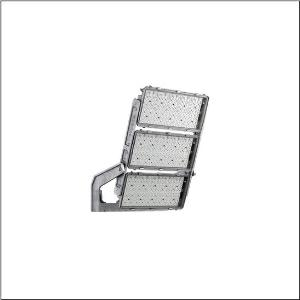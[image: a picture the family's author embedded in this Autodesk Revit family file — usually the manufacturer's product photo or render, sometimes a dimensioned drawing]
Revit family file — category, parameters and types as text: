
# Revit family: floodlight_fl_11_maxi_pro_remote___pl33t_5xa779425t01aa_7d4a
name_source: partatom
category: Lighting Fixtures
units: mm (PartAtom-declared; Revit-internal decimal feet)

## family parameters
Cut with Voids When Loaded = No
Host = Face
Light Source = No
Part Type = Normal
Room Calculation Point = No
Round Connector Dimension = Use Diameter
Shared = No

## types (1)
- --- (1 x LED, 201910 lm, 1539.3 W, 3000K)
    Apparent Load = 1539 VA
    CIE Flux Codes = 27 70 98 100 100
    Color Rendering = 70
    Color Temperature = 3000K
    Default Elevation = 1800 mm
    Description = Floodlight FL 11  maxi  pro Remote floodlight; light control with lens of PMMA; cover panel of toughened safety glass, transparent; light distribution: PL33T, asymmetric direct distribution, LEDcolour temperature: 3000K, rated luminous flux: 201.910lm, colour rendering: CRI > 70, light colour: 730; luminous efficacy: 131lm/W; brightness control: DALI 2 (1 DALI address); with terminal, 8-pole, max. 2.5mm², mains connection: 220..240V/380..400V AC, 50/60Hz, surge voltage resistance: line to ground: 10kV, ECG replaceable separately, no afterglow with DALI off / DMX off command, LED unit replaceable without ESD environment, dustproof LED module, dimming range 10..100%; 1539W floodlight with 2x LED unit of diecast aluminium, coated grey; length: 713mm / width: 651mm / height: 338mm; mounting bracket, of diecast aluminium, uncoated, natural, equipment: Power, protection rating (complete): IP66; insulation class (complete): insulation class I (protective earthing); certification: CE, ENEC, VDE; ball protection: ball impact resistance with accessories, impact resistance: IK07; only for outdoor installations, rated ambient temperature 10°C, permissible operating ambient temperature: -40..+30°C, permissible storage temperature: -40..+85°C; packaging unit: 1 piece

Light Distribution: PL33T
    Height = 320 mm
    Lamp = 1 x LED
    Lamp Light Flux = 201910 lm
    Lamp Power = 1539.3 W
    Lamp count = 1
    Length = 1002 mm
    Luminous efficacy = 131 lm/W
    Manufacturer = Siteco
    ModVariant = No
    Model = 5XA779425T01AA
    Mounting Place = Ceiling
    Mounting Type = Surface mounted
    Number of Poles = 1
    OnlyDefault = Yes
    Power Factor = 1
    Product Name = Floodlight FL 11 maxi pro Remote | PL33T
    Product group = floodlight | ceiling mounted
    ProductGroupID = 302
    Protection Class = Protection class I
    Protection Degree = IP 66
    RLX_Detail_Level = 1
    RLX_Emergency_Light_Flux = 0 lm
    RLX_Emergency_Type = 0
    RLX_Emergency_Type_DB = No
    RlxData = <blob elided: 52485 chars, md5=d2570492>
    Socket = socket
    Standby Power = 0 W
    System Light Flux = 201910 lm
    System Power = 1539 W
    Type Comments = factory setting: luminous flux: 100 % | dim-lin: 254 | 1080 mA
    Type Image = l_1006784.jpg
    URL = http://relux.com
    VarID = @adj_048611
    Voltage = 0 V
    Weight = 0.00 kg
    Width = 655 mm

## geometry (parser evidence)
native form markers: Blend x4, Sweep x12
no freeform markers — native parametric forms only
